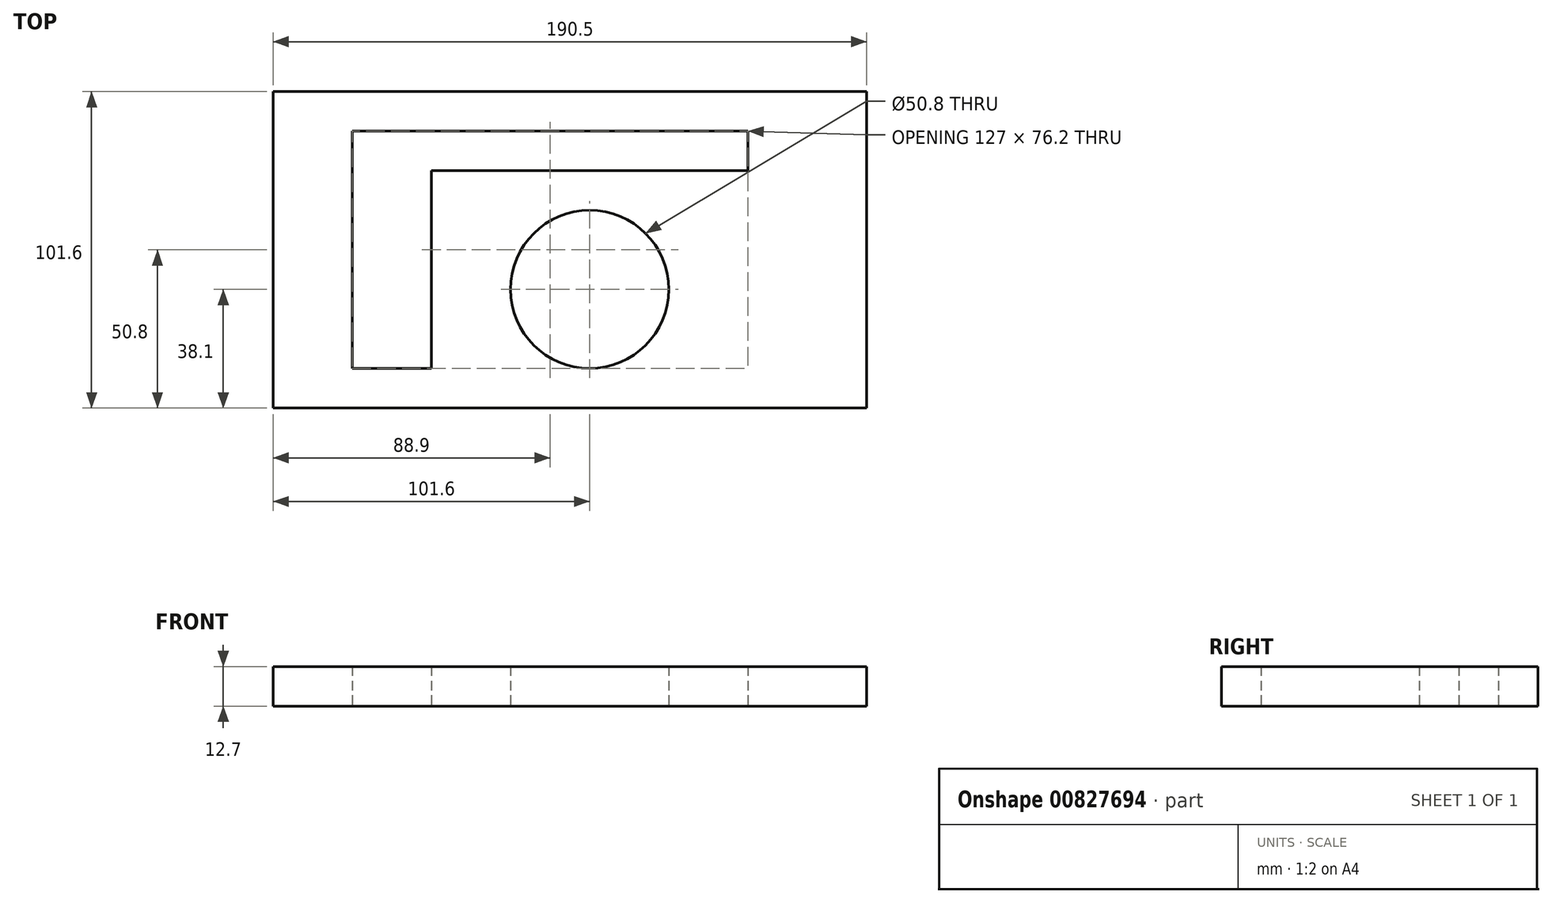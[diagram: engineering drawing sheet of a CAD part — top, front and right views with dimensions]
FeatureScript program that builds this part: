
annotation { "Feature Type Name" : "Feature", "Feature Type Description" : "" }
export const myFeature = defineFeature(function(context is Context, id is Id, definition is map)
    precondition{}
    {
        {
            var Q0;
            Q0=qCreatedBy(makeId("Top.planeOp"),FACE);
            var sketch = newSketch(context, id + "F0", { "sketchPlane" : qUnion([Q0])});
            skLineSegment(sketch, "E0.bottom", {"start": v(-101.6, 63.5) * mm, "end": v(88.9, 63.5) * mm});
            skLineSegment(sketch, "E0.top", {"start": v(-101.6, -38.1) * mm, "end": v(88.9, -38.1) * mm});
            skLineSegment(sketch, "E0.left", {"start": v(-101.6, 63.5) * mm, "end": v(-101.6, -38.1) * mm});
            skLineSegment(sketch, "E0.right", {"start": v(88.9, 63.5) * mm, "end": v(88.9, -38.1) * mm});
            skLineSegment(sketch, "E1.bottom", {"start": v(-76.2, 50.8) * mm, "end": v(-50.8, 50.8) * mm});
            skLineSegment(sketch, "E1.top", {"start": v(-76.2, -25.4) * mm, "end": v(-50.8, -25.4) * mm});
            skLineSegment(sketch, "E1.left", {"start": v(-76.2, 50.8) * mm, "end": v(-76.2, -25.4) * mm});
            skLineSegment(sketch, "E1.right", {"start": v(-50.8, 50.8) * mm, "end": v(-50.8, -25.4) * mm});
            skLineSegment(sketch, "E2.bottom", {"start": v(-50.8, 50.8) * mm, "end": v(50.8, 50.8) * mm});
            skLineSegment(sketch, "E2.top", {"start": v(-50.8, 38.1) * mm, "end": v(50.8, 38.1) * mm});
            skLineSegment(sketch, "E2.left", {"start": v(-50.8, 50.8) * mm, "end": v(-50.8, 38.1) * mm});
            skLineSegment(sketch, "E2.right", {"start": v(50.8, 50.8) * mm, "end": v(50.8, 38.1) * mm});
            skCircle(sketch, "E3", {"center": v(0, 0) * mm, "radius": 25.4 * mm});
            skSolve(sketch);
        }
        {
            var Q0;
            Q0 = qSketchRegion(id + "F0", true);
            extrude(context, id + "F1", {"entities" : qUnion([Q0]), "depth" : 12.7 * mm, "offsetDistance" : 25.4 * mm});
        }
    });
